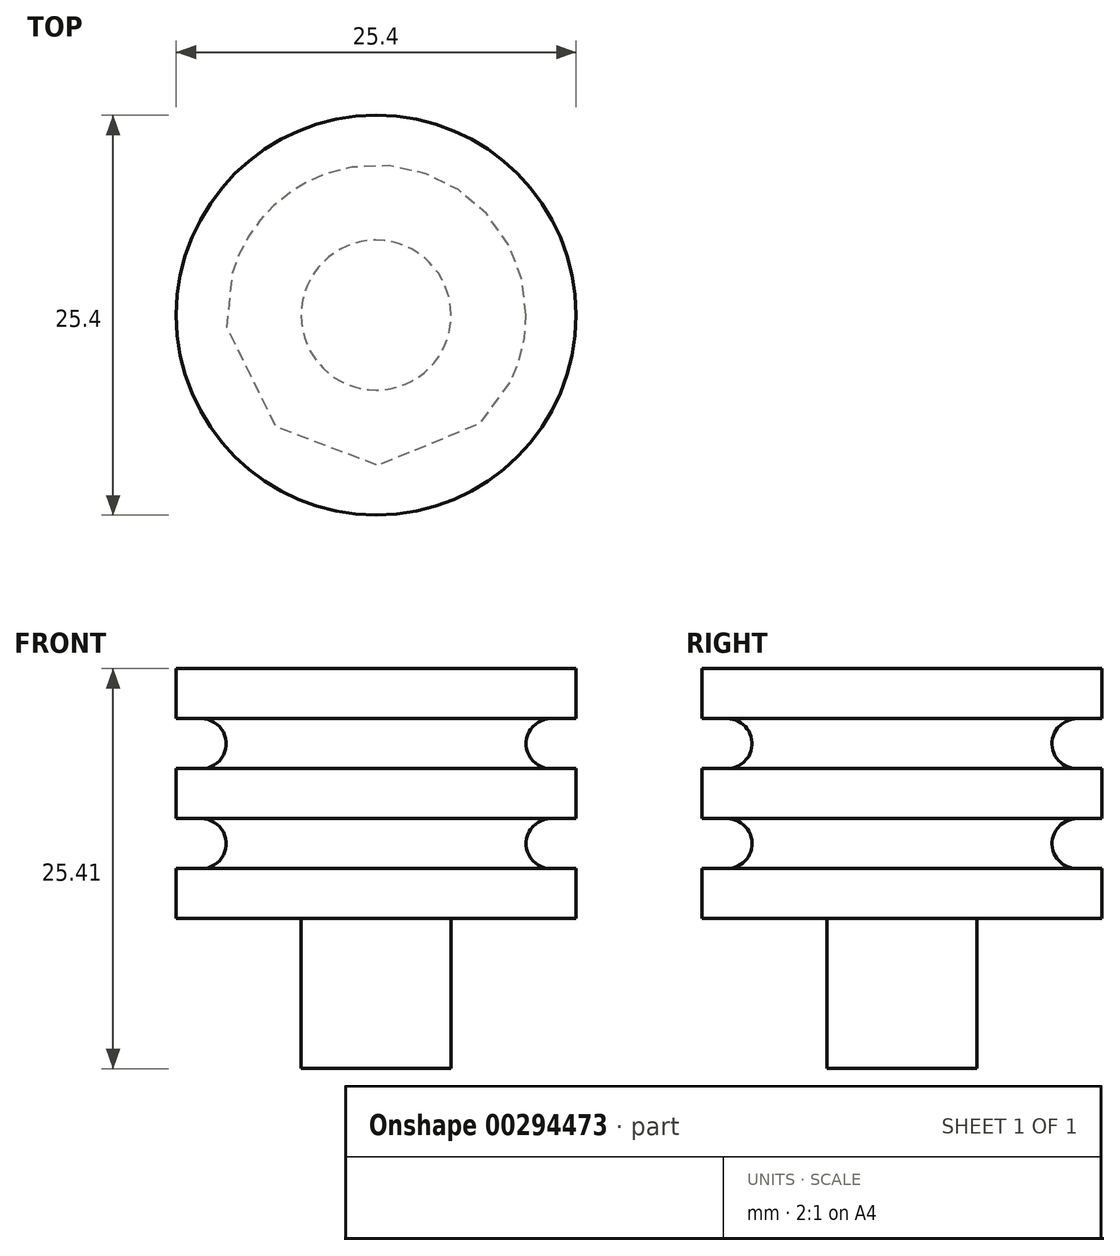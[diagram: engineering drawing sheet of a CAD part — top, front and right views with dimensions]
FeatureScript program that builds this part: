
annotation { "Feature Type Name" : "Feature", "Feature Type Description" : "" }
export const myFeature = defineFeature(function(context is Context, id is Id, definition is map)
    precondition{}
    {
        {
            var Q0;
            Q0=qCreatedBy(makeId("Top.planeOp"),FACE);
            var sketch = newSketch(context, id + "F0", { "sketchPlane" : qUnion([Q0])});
            skCircle(sketch, "E0", {"center": v(0, 0) * mm, "radius": 12.7 * mm});
            skCircle(sketch, "E1", {"center": v(0, 0) * mm, "radius": 4.76 * mm});
            skPoint(sketch, "E2", {"position": v(-12.7, 0) * mm});
            skPoint(sketch, "E3", {"position": v(0, 12.7) * mm});
            skSolve(sketch);
        }
        {
            var Q0;
            Q0=makeQuery(id+"F0.imprint","IMPRINT",FACE,{"disambiguationData":[TD([[makeQuery(id+"F0.imprint","IMPRINT",EDGE,{"derivedFrom":sQuery(id+"F0.wireOp",EDGE,"E0")}),1.0]])]});
            var Q1;
            Q1=makeQuery(id+"F0.imprint","IMPRINT",FACE,{"disambiguationData":[TD([[makeQuery(id+"F0.imprint","IMPRINT",EDGE,{"derivedFrom":sQuery(id+"F0.wireOp",EDGE,"E1")}),1.0]])]});
            extrude(context, id + "F1", {"entities" : qUnion([Q0, Q1]), "depth" : 15.88 * mm});
        }
        {
            var Q0;
            Q0=qCreatedBy(makeId("Front.planeOp"),FACE);
            var sketch = newSketch(context, id + "F2", { "sketchPlane" : qUnion([Q0])});
            skLineSegment(sketch, "E4", {"start": v(0, -76.4) * mm, "end": v(0, 75.84) * mm, "construction": true});
            skSolve(sketch);
        }
        {
            var Q0;
            Q0=makeQuery(id+"F0.imprint","IMPRINT",FACE,{"disambiguationData":[TD([[makeQuery(id+"F0.imprint","IMPRINT",EDGE,{"derivedFrom":sQuery(id+"F0.wireOp",EDGE,"E1")}),1.0]])]});
            extrude(context, id + "F3", {"entities" : qUnion([Q0]), "operationType" : NewBodyOperationType.ADD, "oppositeDirection" : true, "depth" : 9.52 * mm});
        }
        {
            var Q0;
            Q0=qCreatedBy(makeId("Right.planeOp"),FACE);
            var sketch = newSketch(context, id + "F4", { "sketchPlane" : qUnion([Q0])});
            skLineSegment(sketch, "E5.bottom", {"start": v(9.52, 6.35) * mm, "end": v(12.7, 6.35) * mm});
            skLineSegment(sketch, "E5.top", {"start": v(9.53, 3.18) * mm, "end": v(12.7, 3.18) * mm});
            skLineSegment(sketch, "E5.left", {"start": v(9.53, 6.35) * mm, "end": v(9.53, 3.18) * mm});
            skLineSegment(sketch, "E5.right", {"start": v(12.7, 6.35) * mm, "end": v(12.7, 3.18) * mm});
            skLineSegment(sketch, "E6.bottom", {"start": v(9.53, 12.7) * mm, "end": v(12.7, 12.7) * mm});
            skLineSegment(sketch, "E6.top", {"start": v(9.53, 9.53) * mm, "end": v(12.7, 9.53) * mm});
            skLineSegment(sketch, "E6.left", {"start": v(9.53, 12.7) * mm, "end": v(9.53, 9.53) * mm});
            skLineSegment(sketch, "E6.right", {"start": v(12.7, 12.7) * mm, "end": v(12.7, 9.53) * mm});
            skSolve(sketch);
        }
        {
            var Q0;
            Q0 = qSketchRegion(id + "F4", true);
            var Q1;
            Q1=sQuery(id+"F2.wireOp",EDGE,"E4");
            revolve(context, id + "F5", {"operationType" : NewBodyOperationType.REMOVE, "entities" : qUnion([Q0]), "axis" : qUnion([Q1]), "revolveType" : RevolveType.FULL, "oppositeDirection" : true});
        }
        {
            var Q0;
            Q0=makeQuery(id+"F5.boolean.opBoolean","COPY",EDGE,{"derivedFrom":makeQuery(id+"F5.opRevolve","SWEPT_EDGE",EDGE,{"disambiguationData":[OSD([sQuery(id+"F4.wireOp",EDGE,"E5.top"),sQuery(id+"F4.wireOp",EDGE,"E5.left")])]})});
            var Q1;
            Q1=makeQuery(id+"F5.boolean.opBoolean","COPY",EDGE,{"derivedFrom":makeQuery(id+"F5.opRevolve","SWEPT_EDGE",EDGE,{"disambiguationData":[OSD([sQuery(id+"F4.wireOp",EDGE,"E5.bottom"),sQuery(id+"F4.wireOp",EDGE,"E5.left")])]})});
            var Q2;
            Q2=makeQuery(id+"F5.boolean.opBoolean","COPY",EDGE,{"derivedFrom":makeQuery(id+"F5.opRevolve","SWEPT_EDGE",EDGE,{"disambiguationData":[OSD([sQuery(id+"F4.wireOp",EDGE,"E6.top"),sQuery(id+"F4.wireOp",EDGE,"E6.left")])]})});
            var Q3;
            Q3=makeQuery(id+"F5.boolean.opBoolean","COPY",EDGE,{"derivedFrom":makeQuery(id+"F5.opRevolve","SWEPT_EDGE",EDGE,{"disambiguationData":[OSD([sQuery(id+"F4.wireOp",EDGE,"E6.bottom"),sQuery(id+"F4.wireOp",EDGE,"E6.left")])]})});
            fillet(context, id + "F6", {"entities" : qUnion([Q0, Q1, Q2, Q3]), "radius" : 1.59 * mm, "tangentPropagation" : true, "allowEdgeOverflow" : false});
        }
    });
